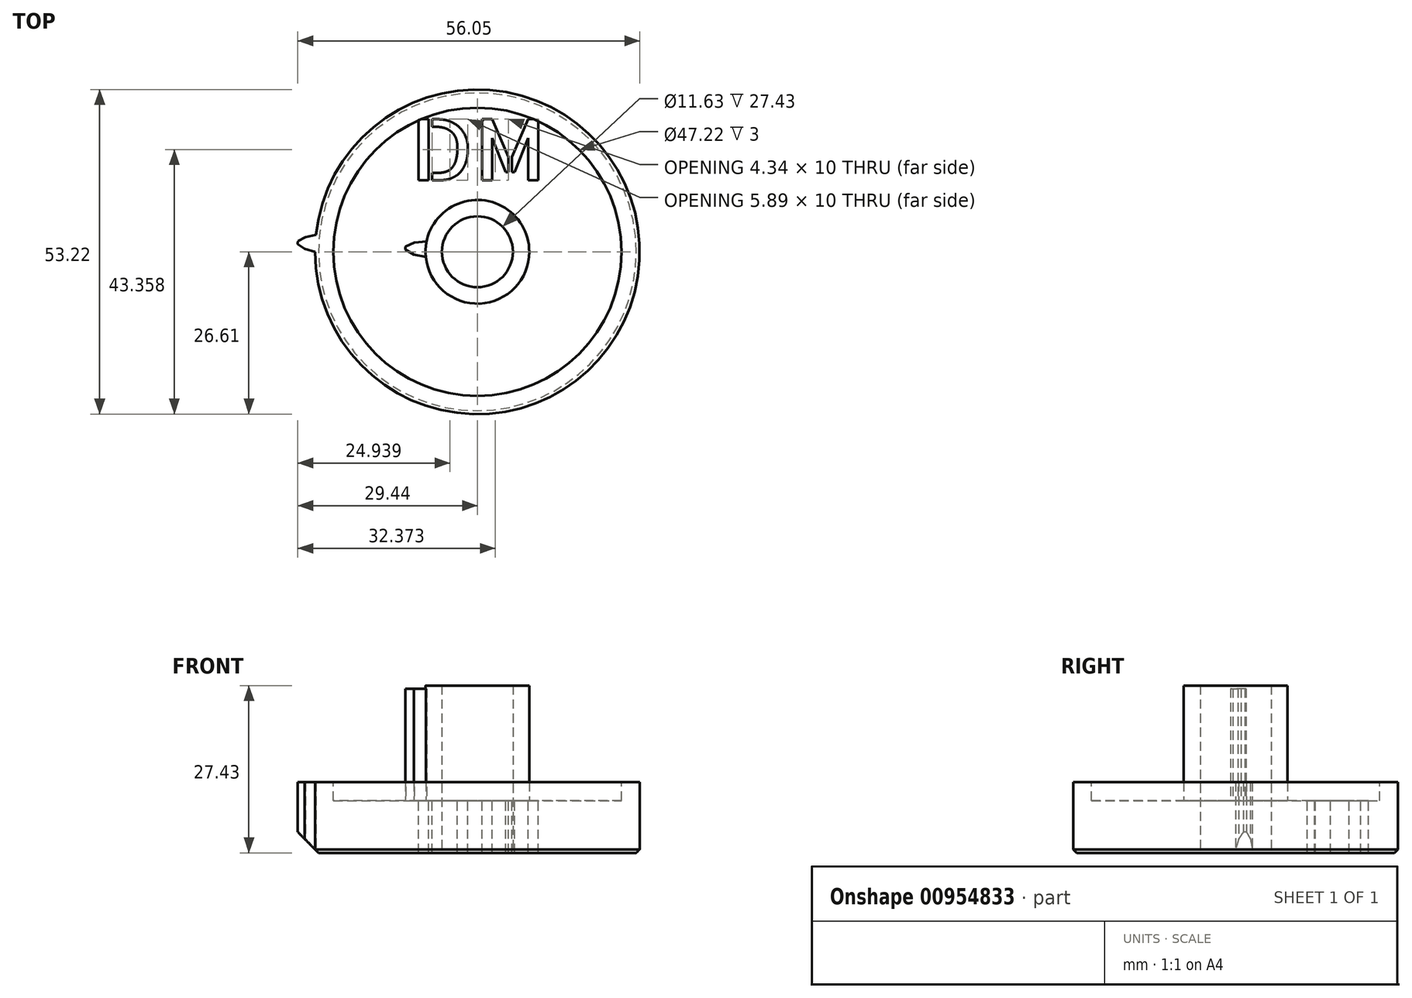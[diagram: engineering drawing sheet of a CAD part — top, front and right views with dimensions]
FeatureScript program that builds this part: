
annotation { "Feature Type Name" : "Feature", "Feature Type Description" : "" }
export const myFeature = defineFeature(function(context is Context, id is Id, definition is map)
    precondition{}
    {
        {
            var Q0;
            Q0=qCreatedBy(makeId("Top.planeOp"),FACE);
            var sketch = newSketch(context, id + "F0", { "sketchPlane" : qUnion([Q0])});
            skCircle(sketch, "E0", {"center": v(0, 0) * mm, "radius": 5.82 * mm});
            skCircle(sketch, "E1", {"center": v(0, 0) * mm, "radius": 8.5 * mm});
            skCircle(sketch, "E2", {"center": v(0, 0) * mm, "radius": 11.8 * mm, "construction": true});
            skCircle(sketch, "E3", {"center": v(0, 0) * mm, "radius": 26.61 * mm});
            skCircle(sketch, "E4", {"center": v(0, 0) * mm, "radius": 29.47 * mm, "construction": true});
            skSolve(sketch);
        }
        {
            var Q0;
            Q0=qCreatedBy(makeId("Top.planeOp"),FACE);
            var sketch = newSketch(context, id + "F1", { "sketchPlane" : qUnion([Q0])});
            skLineSegment(sketch, "E5", {"start": v(-26.61, 0) * mm, "end": v(-28.31, 0.5) * mm});
            skLineSegment(sketch, "E6", {"start": v(-28.31, 0.5) * mm, "end": v(-29.44, 1.27) * mm});
            skLineSegment(sketch, "E7", {"start": v(0, 0) * mm, "end": v(-26.57, 1.38) * mm, "construction": true});
            skArc(sketch, "E8", {"start": v(-29.43, 1.52) * mm, "mid": v(-29.44, 1.4) * mm, "end": v(-29.44, 1.27) * mm});
            skArc(sketch, "E9", {"start": v(-29.44, 1.27) * mm, "mid": v(29.44, -1.4) * mm, "end": v(-29.43, 1.52) * mm, "construction": true});
            skLineSegment(sketch, "E10", {"start": v(-26.57, 1.38) * mm, "end": v(-29.43, 1.52) * mm, "construction": true});
            skArc(sketch, "E11", {"start": v(-26.57, 1.38) * mm, "mid": v(-26.6, 0.69) * mm, "end": v(-26.61, 0) * mm});
            skArc(sketch, "E12", {"start": v(-26.61, 0) * mm, "mid": v(26.6, -0.69) * mm, "end": v(-26.57, 1.38) * mm, "construction": true});
            skArc(sketch, "E13.MirrorCS", {"start": v(-29.43, 1.52) * mm, "mid": v(-29.42, 1.65) * mm, "end": v(-29.42, 1.77) * mm});
            skLineSegment(sketch, "E14.MirrorCS", {"start": v(-28.21, 2.43) * mm, "end": v(-29.42, 1.77) * mm});
            skLineSegment(sketch, "E15.MirrorCS", {"start": v(-26.47, 2.75) * mm, "end": v(-28.21, 2.43) * mm});
            skArc(sketch, "E16.MirrorCS", {"start": v(-26.57, 1.38) * mm, "mid": v(-26.53, 2.06) * mm, "end": v(-26.47, 2.75) * mm});
            skSolve(sketch);
        }
        {
            var Q0;
            Q0=qCreatedBy(makeId("Top.planeOp"),FACE);
            var sketch = newSketch(context, id + "F2", { "sketchPlane" : qUnion([Q0])});
            skLineSegment(sketch, "E17.1", {"start": v(0, 0) * mm, "end": v(-26.57, 1.38) * mm, "construction": true});
            skLineSegment(sketch, "E18", {"start": v(-8.46, -0.81) * mm, "end": v(-10.42, -0.47) * mm});
            skLineSegment(sketch, "E19", {"start": v(-10.42, -0.47) * mm, "end": v(-11.8, 0.36) * mm});
            skArc(sketch, "E20", {"start": v(-11.79, 0.61) * mm, "mid": v(-11.8, 0.49) * mm, "end": v(-11.8, 0.36) * mm});
            skArc(sketch, "E21", {"start": v(-11.8, 0.36) * mm, "mid": v(11.8, -0.49) * mm, "end": v(-11.79, 0.61) * mm, "construction": true});
            skArc(sketch, "E22", {"start": v(-8.49, 0.44) * mm, "mid": v(-8.5, -0.19) * mm, "end": v(-8.46, -0.81) * mm});
            skArc(sketch, "E23", {"start": v(-8.46, -0.81) * mm, "mid": v(8.5, 0.19) * mm, "end": v(-8.49, 0.44) * mm, "construction": true});
            skArc(sketch, "E24.MirrorCS", {"start": v(-11.79, 0.61) * mm, "mid": v(-11.78, 0.74) * mm, "end": v(-11.77, 0.86) * mm});
            skLineSegment(sketch, "E25.MirrorCS", {"start": v(-10.32, 1.54) * mm, "end": v(-11.77, 0.86) * mm});
            skLineSegment(sketch, "E26.MirrorCS", {"start": v(-8.33, 1.68) * mm, "end": v(-10.32, 1.54) * mm});
            skArc(sketch, "E27.MirrorCS", {"start": v(-8.49, 0.44) * mm, "mid": v(-8.43, 1.06) * mm, "end": v(-8.33, 1.68) * mm});
            skSolve(sketch);
        }
        {
            var Q0;
            Q0=makeQuery(id+"F0.imprint","IMPRINT",FACE,{"disambiguationData":[TD([[makeQuery(id+"F0.imprint","IMPRINT",EDGE,{"derivedFrom":sQuery(id+"F0.wireOp",EDGE,"E0")}),-1.0]])]});
            extrude(context, id + "F3", {"entities" : qUnion([Q0]), "depth" : (27.43) * mm, "offsetDistance" : 25 * mm});
        }
        {
            var Q0;
            Q0=makeQuery(id+"F0.imprint","IMPRINT",FACE,{"disambiguationData":[TD([[makeQuery(id+"F0.imprint","IMPRINT",EDGE,{"derivedFrom":sQuery(id+"F0.wireOp",EDGE,"E1")}),-1.0]])]});
            extrude(context, id + "F4", {"entities" : qUnion([Q0]), "operationType" : NewBodyOperationType.ADD, "depth" : 11.57 * mm, "offsetDistance" : 25 * mm});
        }
        {
            var Q0;
            Q0=makeQuery(id+"F4.opExtrude","CAP_FACE",FACE,{"disambiguationData":[OSD([sQuery(id+"F0.wireOp",EDGE,"E1"),sQuery(id+"F0.wireOp",EDGE,"E3")])],"isStart":false});
            var sketch = newSketch(context, id + "F5", { "sketchPlane" : qUnion([Q0])});
            skCircle(sketch, "E28.0", {"center": v(0, 0) * mm, "radius": 26.61 * mm});
            skCircle(sketch, "E29.0", {"center": v(0, 0) * mm, "radius": 23.61 * mm});
            skCircle(sketch, "E30.0", {"center": v(0, 0) * mm, "radius": 8.5 * mm});
            skSolve(sketch);
        }
        {
            var Q0;
            Q0=makeQuery(id+"F5.imprint","IMPRINT",FACE,{"disambiguationData":[TD([[makeQuery(id+"F5.imprint","IMPRINT",EDGE,{"derivedFrom":sQuery(id+"F5.wireOp",EDGE,"E29.0")}),1.0]])]});
            extrude(context, id + "F6", {"entities" : qUnion([Q0]), "operationType" : NewBodyOperationType.REMOVE, "oppositeDirection" : true, "depth" : 3 * mm, "offsetDistance" : 25 * mm});
        }
        {
            var Q0;
            Q0=makeQuery(id+"F1.imprint","IMPRINT",FACE,{"disambiguationData":[TD([[makeQuery(id+"F1.imprint","IMPRINT",EDGE,{"derivedFrom":sQuery(id+"F1.wireOp",EDGE,"E5")}),-1.0]])]});
            var Q1;
            Q1=makeQuery(id+"F4.opExtrude","CAP_FACE",FACE,{"disambiguationData":[OSD([sQuery(id+"F0.wireOp",EDGE,"E1"),sQuery(id+"F0.wireOp",EDGE,"E3")])],"isStart":false});
            extrude(context, id + "F7", {"entities" : qUnion([Q0]), "operationType" : NewBodyOperationType.ADD, "endBound" : BoundingType.UP_TO_SURFACE, "depth" : 25 * mm, "endBoundEntityFace" : qUnion([Q1]), "offsetDistance" : 25 * mm});
        }
        {
            var Q0;
            Q0 = qSketchRegion(id + "F2", true);
            var Q1;
            Q1=makeQuery(id+"F3.opExtrude","CAP_FACE",FACE,{"disambiguationData":[OSD([sQuery(id+"F0.wireOp",EDGE,"E0"),sQuery(id+"F0.wireOp",EDGE,"E1")])],"isStart":false});
            extrude(context, id + "F8", {"entities" : qUnion([Q0]), "operationType" : NewBodyOperationType.ADD, "endBound" : BoundingType.UP_TO_SURFACE, "depth" : 25 * mm, "endBoundEntityFace" : qUnion([Q1]), "hasOffset" : true, "offsetDistance" : .5 * mm});
        }
        {
            var Q0;
            Q0=makeQuery(id+"F6.boolean.opBoolean","COPY",FACE,{"derivedFrom":makeQuery(id+"F6.opExtrude","CAP_FACE",FACE,{"disambiguationData":[OSD([sQuery(id+"F5.wireOp",EDGE,"E29.0"),sQuery(id+"F5.wireOp",EDGE,"E30.0")])],"isStart":false})});
            var sketch = newSketch(context, id + "F9", { "sketchPlane" : qUnion([Q0])});
            skText(sketch, "E31", { "text": "DM\n", "fontName": "AllertaStencil-Regular.ttf"});
            const initialGuessF9  = {"E31": [-0.01093, 0.01175, 1, 0, 0.01]};
            skSetInitialGuess(sketch, initialGuessF9);
            skSolve(sketch);
        }
        {
            var Q0;
            Q0 = qSketchRegion(id + "F9", true);
            extrude(context, id + "F10", {"entities" : qUnion([Q0]), "operationType" : NewBodyOperationType.REMOVE, "endBound" : BoundingType.THROUGH_ALL, "oppositeDirection" : true, "depth" : 1 * mm, "offsetDistance" : 25 * mm});
        }
        {
            var Q0;
            Q0=qCreatedBy(makeId("Right.planeOp"),FACE);
            var sketch = newSketch(context, id + "F11", { "sketchPlane" : qUnion([Q0])});
            skLineSegment(sketch, "E32", {"start": v(26.04, 0) * mm, "end": v(29.54, 0) * mm});
            skLineSegment(sketch, "E33", {"start": v(29.54, 0) * mm, "end": v(29.54, 3.5) * mm});
            skLineSegment(sketch, "E34", {"start": v(29.54, 3.5) * mm, "end": v(26.04, 0) * mm});
            skSolve(sketch);
        }
        {
            var Q0;
            Q0 = qSketchRegion(id + "F11", true);
            var Q1;
            Q1=makeQuery(id+"F3.opExtrude","CAP_EDGE",EDGE,{"disambiguationData":[OSD([sQuery(id+"F0.wireOp",EDGE,"E0")])],"isStart":true});
            revolve(context, id + "F12", {"operationType" : NewBodyOperationType.REMOVE, "surfaceOperationType" : NewSurfaceOperationType.NEW, "entities" : qUnion([Q0]), "axis" : qUnion([Q1]), "revolveType" : RevolveType.FULL, "oppositeDirection" : true});
        }
    });
